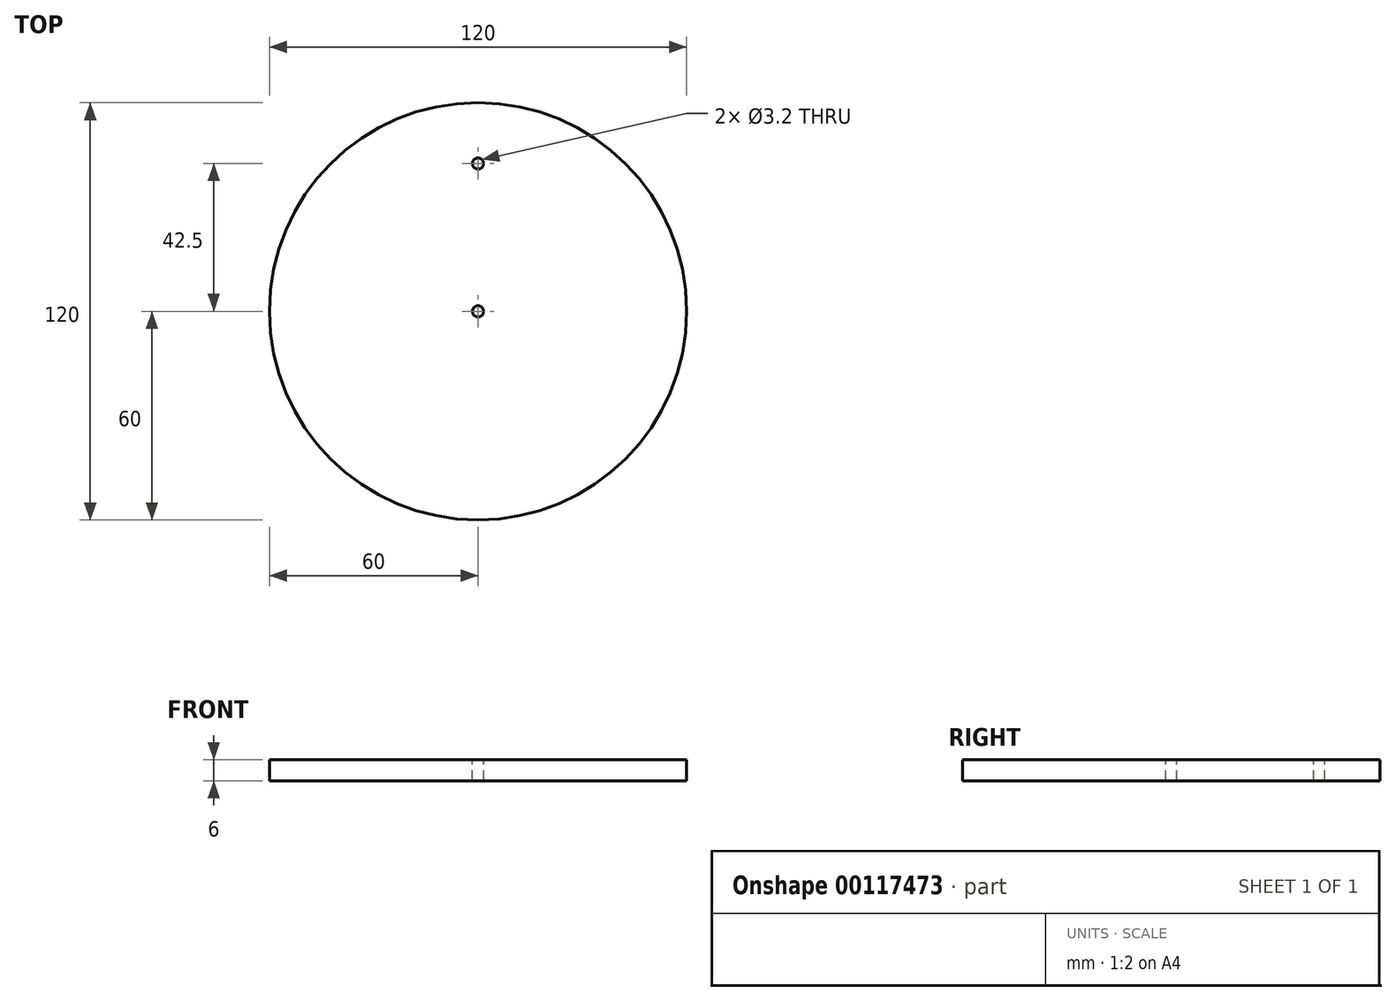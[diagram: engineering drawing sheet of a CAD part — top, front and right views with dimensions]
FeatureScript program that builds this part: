
annotation { "Feature Type Name" : "Feature", "Feature Type Description" : "" }
export const myFeature = defineFeature(function(context is Context, id is Id, definition is map)
    precondition{}
    {
        {
            var Q0;
            Q0=qCreatedBy(makeId("Top.planeOp"),FACE);
            var sketch = newSketch(context, id + "F0", { "sketchPlane" : qUnion([Q0])});
            skCircle(sketch, "E0", {"center": v(0, 0) * mm, "radius": 60 * mm});
            skSolve(sketch);
        }
        {
            var Q0;
            Q0 = qSketchRegion(id + "F0", true);
            extrude(context, id + "F1", {"entities" : qUnion([Q0]), "depth" : 6 * mm});
        }
        {
            var Q0;
            Q0=makeQuery(id+"F1.opExtrude","CAP_FACE",FACE,{"disambiguationData":[OSD([sQuery(id+"F0.wireOp",EDGE,"E0")])],"isStart":false});
            var sketch = newSketch(context, id + "F2", { "sketchPlane" : qUnion([Q0])});
            skPoint(sketch, "E1", {"position": v(0, 0) * mm});
            skSolve(sketch);
        }
        {
            var Q0;
            Q0=sQuery(id+"F2.wireOp",VERTEX,"E1");
            var Q1;
            Q1=makeQuery(id+"F1.opExtrude","SWEPT_BODY",BODY,{"disambiguationData":[OSD([sQuery(id+"F0.wireOp",EDGE,"E0")])]});
            hole(context, id + "F3", {"style" : HoleStyle.SIMPLE, "endStyle" : HoleEndStyle.THROUGH, "standardTappedOrClearance" : lookupTablePath({ "standard" : "ISO", "engagement" : "75%", "pitch" : "0.75 mm", "size" : "M4", "type" : "Tapped" }), "standardBlindInLast" : lookupTablePath({ "standard" : "ISO", "engagement" : "75%", "pitch" : "0.75 mm", "size" : "M4", "type" : "Tapped" }), "holeDiameter" : 3.2 * mm, "locations" : qUnion([Q0]), "scope" : qUnion([Q1]), "isTappedThrough" : true, "showTappedDepth" : true});
        }
        {
            var Q0;
            Q0=makeQuery(id+"F1.opExtrude","CAP_FACE",FACE,{"disambiguationData":[OSD([sQuery(id+"F0.wireOp",EDGE,"E0")])],"isStart":false});
            var sketch = newSketch(context, id + "F4", { "sketchPlane" : qUnion([Q0])});
            skLineSegment(sketch, "E2", {"start": v(0, 0) * mm, "end": v(0, 60) * mm});
            skSolve(sketch);
        }
        {
            var Q0;
            Q0=makeQuery(id+"F4.imprint","IMPRINT",FACE,{"disambiguationData":[TD([[makeQuery(id+"F4.imprint","IMPRINT",EDGE,{"derivedFrom":makeQuery(id+"F1.opExtrude","CAP_EDGE",EDGE,{"disambiguationData":[OSD([sQuery(id+"F0.wireOp",EDGE,"E0")])],"isStart":false})}),1.0]])]});
            var sketch = newSketch(context, id + "F5", { "sketchPlane" : qUnion([Q0])});
            skPoint(sketch, "E3", {"position": v(0, 42.5) * mm});
            skSolve(sketch);
        }
        {
            var Q0;
            Q0=sQuery(id+"F5.wireOp",VERTEX,"E3");
            var Q1;
            Q1=makeQuery(id+"F1.opExtrude","SWEPT_BODY",BODY,{"disambiguationData":[OSD([sQuery(id+"F0.wireOp",EDGE,"E0")])]});
            hole(context, id + "F6", {"style" : HoleStyle.SIMPLE, "endStyle" : HoleEndStyle.THROUGH, "standardTappedOrClearance" : lookupTablePath({ "standard" : "ISO", "engagement" : "75%", "pitch" : "0.75 mm", "size" : "M4", "type" : "Tapped" }), "standardBlindInLast" : lookupTablePath({ "standard" : "ISO", "engagement" : "75%", "pitch" : "0.75 mm", "size" : "M4", "type" : "Tapped" }), "holeDiameter" : 3.2 * mm, "locations" : qUnion([Q0]), "scope" : qUnion([Q1]), "isTappedThrough" : true, "showTappedDepth" : true});
        }
    });
